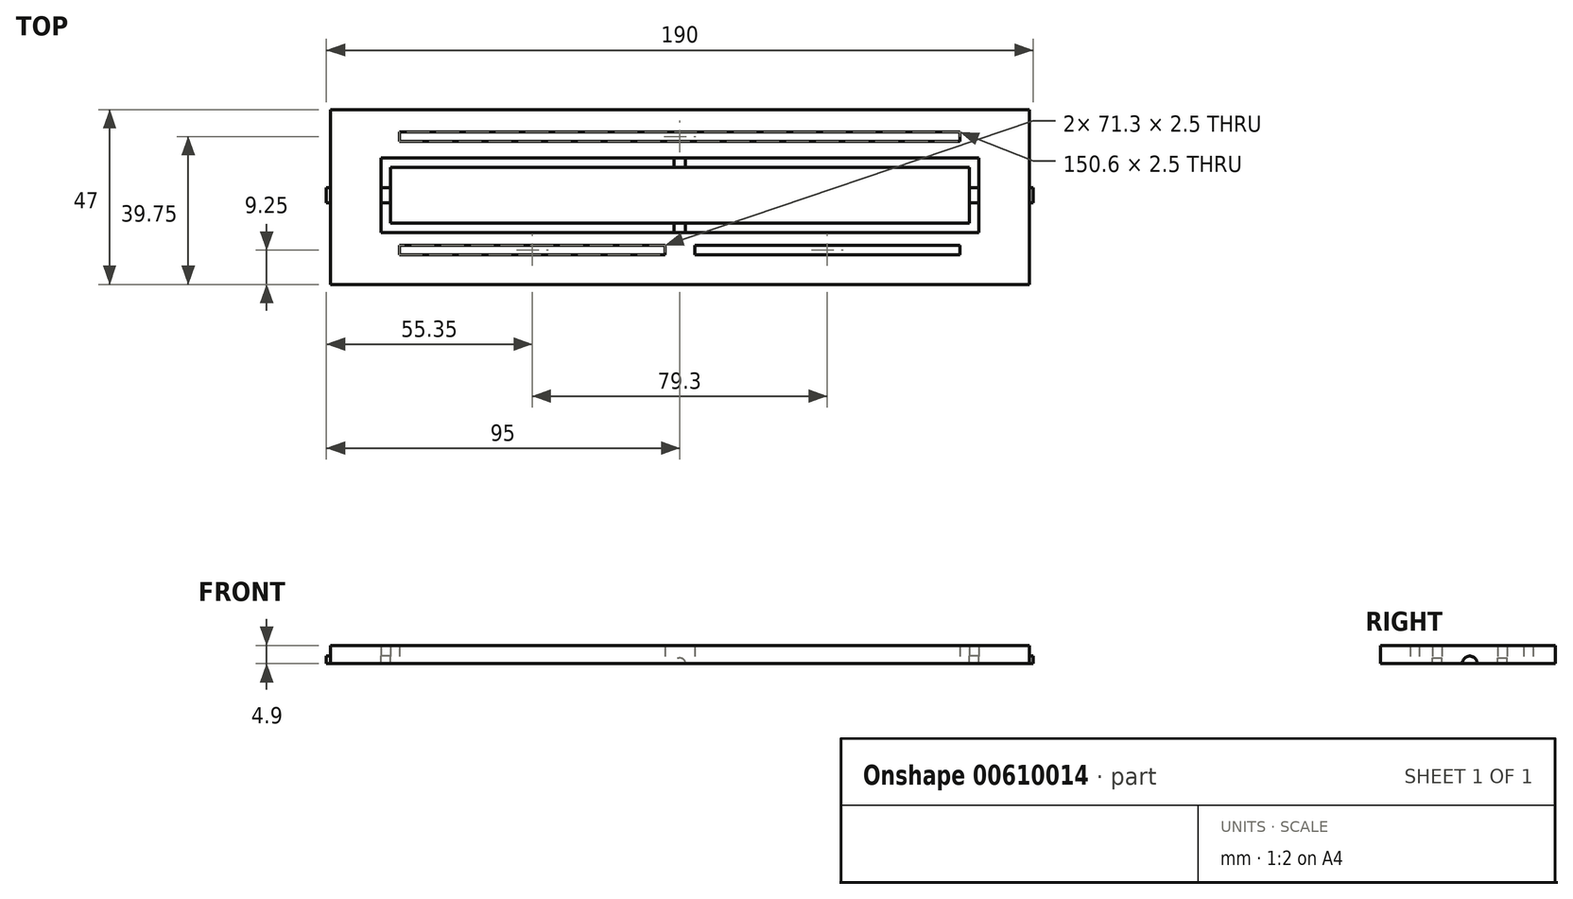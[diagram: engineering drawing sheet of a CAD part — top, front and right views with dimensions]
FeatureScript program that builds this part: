
annotation { "Feature Type Name" : "Feature", "Feature Type Description" : "" }
export const myFeature = defineFeature(function(context is Context, id is Id, definition is map)
    precondition{}
    {
        {
            var Q0;
            Q0=qCreatedBy(makeId("Front.planeOp"),FACE);
            var sketch = newSketch(context, id + "F0", { "sketchPlane" : qUnion([Q0])});
            skPoint(sketch, "E0.middle", {"position": v(0.08, 0) * mm});
            skLineSegment(sketch, "E1", {"start": v(-79.42, 0) * mm, "end": v(79.18, 0) * mm});
            skLineSegment(sketch, "E2.bottom", {"start": v(-79.42, 0) * mm, "end": v(-95.32, 0) * mm});
            skLineSegment(sketch, "E2.right", {"start": v(-95.32, 0) * mm, "end": v(-95.32, 4.75) * mm});
            skLineSegment(sketch, "E3", {"start": v(-79.42, 1) * mm, "end": v(-95.32, 4.75) * mm});
            skLineSegment(sketch, "E4.bottom", {"start": v(79.18, 0) * mm, "end": v(95.08, 0) * mm});
            skLineSegment(sketch, "E4.right", {"start": v(95.08, 0) * mm, "end": v(95.08, 4.75) * mm});
            skLineSegment(sketch, "E5", {"start": v(79.18, 1) * mm, "end": v(95.08, 4.75) * mm});
            skLineSegment(sketch, "E6.bottom", {"start": v(-95.32, 0) * mm, "end": v(95.08, 0) * mm});
            skLineSegment(sketch, "E6.top", {"start": v(-95.32, 4.75) * mm, "end": v(95.08, 4.75) * mm});
            skArc(sketch, "E7", {"start": v(1.5, 0) * mm, "mid": v(0, 1.5) * mm, "end": v(-1.5, 0) * mm});
            skLineSegment(sketch, "E8", {"start": v(-1.5, 0) * mm, "end": v(1.5, 0) * mm});
            skLineSegment(sketch, "E9", {"start": v(0, 0) * mm, "end": v(0, 4.75) * mm});
            skArc(sketch, "E10", {"start": v(79.18, 1) * mm, "mid": v(-0.12, 4.75) * mm, "end": v(-79.42, 1) * mm});
            skSolve(sketch);
        }
        {
            var Q0;
            Q0=qCreatedBy(makeId("Front.planeOp"),FACE);
            var sketch = newSketch(context, id + "F1", { "sketchPlane" : qUnion([Q0])});
            skLineSegment(sketch, "E11.bottom", {"start": v(0, 0) * mm, "end": v(-93.92, 0) * mm});
            skLineSegment(sketch, "E11.top", {"start": v(0, 4.9) * mm, "end": v(-93.92, 4.9) * mm});
            skLineSegment(sketch, "E11.right", {"start": v(-93.92, 0) * mm, "end": v(-93.92, 4.9) * mm});
            skLineSegment(sketch, "E12.top", {"start": v(0, 4.9) * mm, "end": v(93.92, 4.9) * mm});
            skLineSegment(sketch, "E12.right", {"start": v(93.92, 0) * mm, "end": v(93.92, 4.9) * mm});
            skLineSegment(sketch, "E13", {"start": v(0, 0) * mm, "end": v(93.92, 0) * mm});
            skSolve(sketch);
        }
        {
            var Q0;
            Q0=qCreatedBy(makeId("Top.planeOp"),FACE);
            var sketch = newSketch(context, id + "F2", { "sketchPlane" : qUnion([Q0])});
            skPoint(sketch, "E14.middle", {"position": v(0, 0) * mm});
            skLineSegment(sketch, "E15.right", {"start": v(75.3, 17) * mm, "end": v(75.3, 14.5) * mm});
            skLineSegment(sketch, "E16.right", {"start": v(75.3, -13.5) * mm, "end": v(75.3, -16) * mm});
            skLineSegment(sketch, "E17.right", {"start": v(4, -13.5) * mm, "end": v(4, -16) * mm});
            skLineSegment(sketch, "E18.right", {"start": v(-4, -13.5) * mm, "end": v(-4, -16) * mm});
            skLineSegment(sketch, "E19.right", {"start": v(-75.3, -13.5) * mm, "end": v(-75.3, -16) * mm});
            skLineSegment(sketch, "E20.right", {"start": v(-75.3, 17) * mm, "end": v(-75.3, 14.5) * mm});
            skLineSegment(sketch, "E21", {"start": v(4, -13.5) * mm, "end": v(75.3, -13.5) * mm});
            skLineSegment(sketch, "E22", {"start": v(75.3, -16) * mm, "end": v(4, -16) * mm});
            skLineSegment(sketch, "E23", {"start": v(-75.3, -16) * mm, "end": v(-4, -16) * mm});
            skLineSegment(sketch, "E24", {"start": v(-4, -13.5) * mm, "end": v(-75.3, -13.5) * mm});
            skLineSegment(sketch, "E25", {"start": v(-75.3, 14.5) * mm, "end": v(75.3, 14.5) * mm});
            skLineSegment(sketch, "E26", {"start": v(75.3, 17) * mm, "end": v(-75.3, 17) * mm});
            skLineSegment(sketch, "E27.bottom", {"start": v(-80.3, 10) * mm, "end": v(80.3, 10) * mm});
            skLineSegment(sketch, "E27.top", {"start": v(-80.3, -10) * mm, "end": v(80.3, -10) * mm});
            skLineSegment(sketch, "E27.left", {"start": v(-80.3, 10) * mm, "end": v(-80.3, -10) * mm});
            skLineSegment(sketch, "E27.right", {"start": v(80.3, 10) * mm, "end": v(80.3, -10) * mm});
            skLineSegment(sketch, "E28.0", {"start": v(-77.8, 7.5) * mm, "end": v(77.8, 7.5) * mm});
            skLineSegment(sketch, "E28.1", {"start": v(-77.8, 7.5) * mm, "end": v(-77.8, -7.5) * mm});
            skLineSegment(sketch, "E28.2", {"start": v(-77.8, -7.5) * mm, "end": v(77.8, -7.5) * mm});
            skLineSegment(sketch, "E28.3", {"start": v(77.8, 7.5) * mm, "end": v(77.8, -7.5) * mm});
            skSolve(sketch);
        }
        {
            var Q0;
            Q0 = qSketchRegion(id + "F1", true);
            extrude(context, id + "F3", {"entities" : qUnion([Q0]), "depth" : 24 * mm, "offsetDistance" : 25 * mm, "hasSecondDirection" : true, "secondDirectionOppositeDirection" : true, "secondDirectionDepth" : 23 * mm});
        }
        {
            var Q0;
            Q0 = qSketchRegion(id + "F2", true);
            extrude(context, id + "F4", {"entities" : qUnion([Q0]), "operationType" : NewBodyOperationType.REMOVE, "endBound" : BoundingType.UP_TO_NEXT, "depth" : 5 * mm, "offsetDistance" : 25 * mm});
        }
        {
            var Q0;
            {var subQ4=sQuery(id+"F0.wireOp",EDGE,"E2.right");var subQ5=sQuery(id+"F0.wireOp",EDGE,"E6.top");Q0=makeQuery(id+"F4.boolean.opBoolean","SPLIT",FACE,{"disambiguationData":[TD([makeQuery(id+"FFEDnVLw38i4Ooj_0.opExtrude","SWEPT_FACE",FACE,{"disambiguationData":[OSD([subQ4])]})])],"derivedFrom":makeQuery(id+"FFEDnVLw38i4Ooj_0.opExtrude","SWEPT_FACE",FACE,{"disambiguationData":[OSD([subQ5])]})});}
            var sketch = newSketch(context, id + "F5", { "sketchPlane" : qUnion([Q0])});
            skLineSegment(sketch, "E29.bottom", {"start": v(-80.3, 10) * mm, "end": v(-82.3, 10) * mm});
            skLineSegment(sketch, "E29.top", {"start": v(-80.3, -10) * mm, "end": v(-82.3, -10) * mm});
            skLineSegment(sketch, "E29.left", {"start": v(-80.3, 10) * mm, "end": v(-80.3, -10) * mm});
            skLineSegment(sketch, "E29.right", {"start": v(-82.3, 10) * mm, "end": v(-82.3, -10) * mm});
            skLineSegment(sketch, "E30.bottom", {"start": v(80.3, 10) * mm, "end": v(82.3, 10) * mm});
            skLineSegment(sketch, "E30.top", {"start": v(80.3, -10) * mm, "end": v(82.3, -10) * mm});
            skLineSegment(sketch, "E30.left", {"start": v(80.3, 10) * mm, "end": v(80.3, -10) * mm});
            skLineSegment(sketch, "E30.right", {"start": v(82.3, 10) * mm, "end": v(82.3, -10) * mm});
            skSolve(sketch);
        }
        {
            var Q0;
            Q0=qCreatedBy(makeId("Right.planeOp"),FACE);
            var sketch = newSketch(context, id + "F6", { "sketchPlane" : qUnion([Q0])});
            skArc(sketch, "E31", {"start": v(2, 0) * mm, "mid": v(0, 2) * mm, "end": v(-2, 0) * mm});
            skLineSegment(sketch, "E32", {"start": v(-2, 0) * mm, "end": v(2, 0) * mm});
            skSolve(sketch);
        }
        {
            var Q0;
            Q0 = qSketchRegion(id + "F6", true);
            extrude(context, id + "F7", {"entities" : qUnion([Q0]), "operationType" : NewBodyOperationType.ADD, "depth" : 95 * mm, "offsetDistance" : 25 * mm, "hasSecondDirection" : true, "secondDirectionOppositeDirection" : true, "secondDirectionDepth" : 95 * mm});
        }
        {
            var Q0;
            Q0=makeQuery(id+"F0.imprint","IMPRINT",FACE,{"disambiguationData":[TD([[makeQuery(id+"F0.imprint","IMPRINT",EDGE,{"derivedFrom":sQuery(id+"F0.wireOp",EDGE,"E7")}),1.0]])]});
            extrude(context, id + "F8", {"entities" : qUnion([Q0]), "operationType" : NewBodyOperationType.ADD, "depth" : 12 * mm, "offsetDistance" : 25 * mm, "hasSecondDirection" : true, "secondDirectionOppositeDirection" : true, "secondDirectionDepth" : 12 * mm});
        }
        {
            var Q0;
            Q0=makeQuery(id+"F2.imprint","IMPRINT",FACE,{"disambiguationData":[TD([[makeQuery(id+"F2.imprint","IMPRINT",EDGE,{"derivedFrom":sQuery(id+"F2.wireOp",EDGE,"E28.0")}),-1.0]])]});
            extrude(context, id + "F9", {"entities" : qUnion([Q0]), "operationType" : NewBodyOperationType.ADD, "depth" : 4.75 * mm, "offsetDistance" : 25 * mm});
        }
    });
